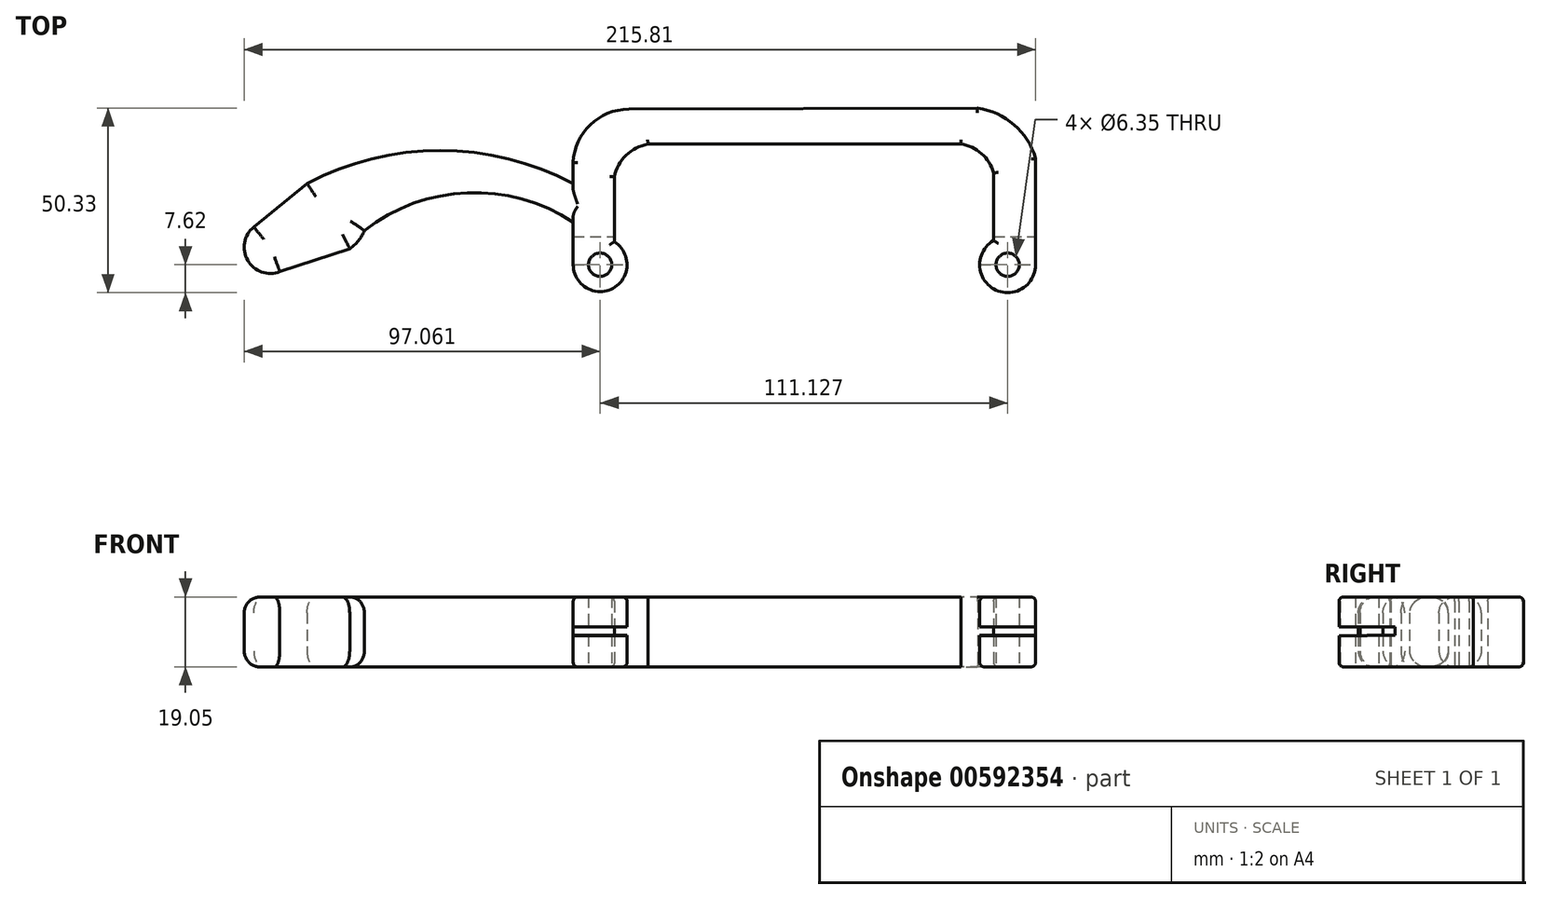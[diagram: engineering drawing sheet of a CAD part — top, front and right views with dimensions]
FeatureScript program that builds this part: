
annotation { "Feature Type Name" : "Feature", "Feature Type Description" : "" }
export const myFeature = defineFeature(function(context is Context, id is Id, definition is map)
    precondition{}
    {
        {
            var Q0;
            Q0=qCreatedBy(makeId("Top.planeOp"),FACE);
            var sketch = newSketch(context, id + "F0", { "sketchPlane" : qUnion([Q0])});
            skArc(sketch, "E0", {"start": v(-64.35, 0) * mm, "mid": v(-53.45, -6.42) * mm, "end": v(-53.12, 6.22) * mm});
            skArc(sketch, "E1", {"start": v(50.28, 6.58) * mm, "mid": v(50.32, -6.6) * mm, "end": v(61.74, 0) * mm});
            skLineSegment(sketch, "E2", {"start": v(-49.2, 42.4) * mm, "end": v(45.92, 42.71) * mm});
            skLineSegment(sketch, "E3", {"start": v(-64.35, 0) * mm, "end": v(-64.36, 11.6) * mm});
            skLineSegment(sketch, "E4", {"start": v(61.74, 0) * mm, "end": v(61.74, 29) * mm});
            skLineSegment(sketch, "E5", {"start": v(-53.12, 6.22) * mm, "end": v(-53.12, 23.94) * mm});
            skLineSegment(sketch, "E6", {"start": v(50.28, 6.58) * mm, "end": v(50.28, 25.02) * mm});
            skLineSegment(sketch, "E7", {"start": v(-43.96, 32.9) * mm, "end": v(41.35, 32.9) * mm});
            skArc(sketch, "E8", {"start": v(-43.96, 32.9) * mm, "mid": v(-49.93, 29.85) * mm, "end": v(-53.12, 23.94) * mm});
            skArc(sketch, "E9", {"start": v(50.28, 25.02) * mm, "mid": v(45.78, 31.23) * mm, "end": v(38.3, 32.9) * mm});
            skCircle(sketch, "E10", {"center": v(-57, 0) * mm, "radius": 3.18 * mm});
            skCircle(sketch, "E11", {"center": v(54.12, 0) * mm, "radius": 3.18 * mm});
            skArc(sketch, "E12", {"start": v(-49.2, 42.4) * mm, "mid": v(-59.68, 38.2) * mm, "end": v(-64.37, 27.92) * mm});
            skPoint(sketch, "E13.orphan", {"position": v(50.28, 19.35) * mm});
            skPoint(sketch, "E14.orphan", {"position": v(50.28, 4) * mm});
            skPoint(sketch, "E15.orphan", {"position": v(-53.12, 32.9) * mm});
            skPoint(sketch, "E16.orphan", {"position": v(-53.12, 19.57) * mm});
            skPoint(sketch, "E17.trimOffspring.end.orphan", {"position": v(50.28, 34.71) * mm});
            skArc(sketch, "E18", {"start": v(61.74, 29) * mm, "mid": v(55.85, 38.18) * mm, "end": v(45.92, 42.71) * mm});
            skArc(sketch, "E19", {"start": v(-64.37, 22.19) * mm, "mid": v(-100.65, 31.15) * mm, "end": v(-136.94, 22.19) * mm});
            skArc(sketch, "E20", {"start": v(-125.3, 4.38) * mm, "mid": v(-122.93, 6.54) * mm, "end": v(-121.32, 9.32) * mm});
            skPoint(sketch, "E20.second.point", {"position": v(-136.94, 4.23) * mm});
            skPoint(sketch, "E20.third.point", {"position": v(-120.6, 13.98) * mm});
            skArc(sketch, "E21", {"start": v(-151.44, 10.3) * mm, "mid": v(-153.1, 1.17) * mm, "end": v(-144.36, -1.88) * mm});
            skArc(sketch, "E22", {"start": v(-64.36, 11.6) * mm, "mid": v(-93.2, 19.62) * mm, "end": v(-121.32, 9.32) * mm});
            skLineSegment(sketch, "E23", {"start": v(-151.44, 10.3) * mm, "end": v(-136.94, 22.19) * mm});
            skLineSegment(sketch, "E24", {"start": v(-145.09, -2.12) * mm, "end": v(-125.3, 4.38) * mm});
            skLineSegment(sketch, "E25.trimOffspring", {"start": v(-64.37, 22.19) * mm, "end": v(-64.37, 27.92) * mm});
            skSolve(sketch);
        }
        {
            var Q0;
            Q0 = qSketchRegion(id + "F0", true);
            extrude(context, id + "F1", {"entities" : qUnion([Q0]), "depth" : 19.05 * mm, "offsetDistance" : 25.4 * mm});
        }
        {
            var Q0;
            Q0=makeQuery(id+"F1.opExtrude","CAP_EDGE",EDGE,{"disambiguationData":[OSD([sQuery(id+"F0.wireOp",EDGE,"E22")])],"isStart":false});
            var Q1;
            Q1=makeQuery(id+"F1.opExtrude","CAP_EDGE",EDGE,{"disambiguationData":[OSD([sQuery(id+"F0.wireOp",EDGE,"E20")])],"isStart":false});
            var Q2;
            Q2=makeQuery(id+"F1.opExtrude","CAP_EDGE",EDGE,{"disambiguationData":[OSD([sQuery(id+"F0.wireOp",EDGE,"E23")])],"isStart":false});
            var Q3;
            Q3=makeQuery(id+"F1.opExtrude","CAP_EDGE",EDGE,{"disambiguationData":[OSD([sQuery(id+"F0.wireOp",EDGE,"E21")])],"isStart":false});
            var Q4;
            Q4=makeQuery(id+"F1.opExtrude","CAP_EDGE",EDGE,{"disambiguationData":[OSD([sQuery(id+"F0.wireOp",EDGE,"E19")])],"isStart":false});
            fillet(context, id + "F2", {"entities" : qUnion([Q0, Q1, Q2, Q3, Q4]), "radius" : 4.32 * mm, "tangentPropagation" : true, "allowEdgeOverflow" : false});
        }
        {
            var Q0;
            Q0=makeQuery(id+"F1.opExtrude","CAP_EDGE",EDGE,{"disambiguationData":[OSD([sQuery(id+"F0.wireOp",EDGE,"E24")])],"isStart":true});
            var Q1;
            Q1=makeQuery(id+"F1.opExtrude","CAP_EDGE",EDGE,{"disambiguationData":[OSD([sQuery(id+"F0.wireOp",EDGE,"E20")])],"isStart":true});
            var Q2;
            Q2=makeQuery(id+"F1.opExtrude","CAP_EDGE",EDGE,{"disambiguationData":[OSD([sQuery(id+"F0.wireOp",EDGE,"E22")])],"isStart":true});
            var Q3;
            Q3=makeQuery(id+"F1.opExtrude","CAP_EDGE",EDGE,{"disambiguationData":[OSD([sQuery(id+"F0.wireOp",EDGE,"E21")])],"isStart":true});
            var Q4;
            Q4=makeQuery(id+"F1.opExtrude","CAP_EDGE",EDGE,{"disambiguationData":[OSD([sQuery(id+"F0.wireOp",EDGE,"E19")])],"isStart":true});
            var Q5;
            Q5=makeQuery(id+"F1.opExtrude","CAP_EDGE",EDGE,{"disambiguationData":[OSD([sQuery(id+"F0.wireOp",EDGE,"E23")])],"isStart":true});
            fillet(context, id + "F3", {"entities" : qUnion([Q0, Q1, Q2, Q3, Q4, Q5]), "radius" : 4.32 * mm, "tangentPropagation" : true, "allowEdgeOverflow" : false});
        }
        {
            var Q0;
            Q0=makeQuery(id+"F1.opExtrude","CAP_EDGE",EDGE,{"disambiguationData":[OSD([sQuery(id+"F0.wireOp",EDGE,"E12")])],"isStart":true});
            var Q1;
            Q1=makeQuery(id+"F1.opExtrude","CAP_EDGE",EDGE,{"disambiguationData":[OSD([sQuery(id+"F0.wireOp",EDGE,"E2")])],"isStart":true});
            var Q2;
            Q2=makeQuery(id+"F1.opExtrude","CAP_EDGE",EDGE,{"disambiguationData":[OSD([sQuery(id+"F0.wireOp",EDGE,"E6")])],"isStart":true});
            var Q3;
            Q3=makeQuery(id+"F1.opExtrude","CAP_EDGE",EDGE,{"disambiguationData":[OSD([sQuery(id+"F0.wireOp",EDGE,"E9")])],"isStart":true});
            var Q4;
            Q4=makeQuery(id+"F1.opExtrude","CAP_EDGE",EDGE,{"disambiguationData":[OSD([sQuery(id+"F0.wireOp",EDGE,"E5")])],"isStart":true});
            var Q5;
            Q5=makeQuery(id+"F1.opExtrude","CAP_EDGE",EDGE,{"disambiguationData":[OSD([sQuery(id+"F0.wireOp",EDGE,"E8")])],"isStart":true});
            var Q6;
            Q6=makeQuery(id+"F1.opExtrude","CAP_EDGE",EDGE,{"disambiguationData":[OSD([sQuery(id+"F0.wireOp",EDGE,"E7")])],"isStart":true});
            var Q7;
            Q7=makeQuery(id+"F1.opExtrude","CAP_EDGE",EDGE,{"disambiguationData":[OSD([sQuery(id+"F0.wireOp",EDGE,"E18")])],"isStart":true});
            var Q8;
            Q8=makeQuery(id+"F1.opExtrude","CAP_EDGE",EDGE,{"disambiguationData":[OSD([sQuery(id+"F0.wireOp",EDGE,"E4")])],"isStart":true});
            var Q9;
            Q9=makeQuery(id+"F1.opExtrude","CAP_EDGE",EDGE,{"disambiguationData":[OSD([sQuery(id+"F0.wireOp",EDGE,"E3")])],"isStart":true});
            var Q10;
            Q10=makeQuery(id+"F1.opExtrude","CAP_EDGE",EDGE,{"disambiguationData":[OSD([sQuery(id+"F0.wireOp",EDGE,"E0")])],"isStart":true});
            fillet(context, id + "F4", {"entities" : qUnion([Q0, Q1, Q2, Q3, Q4, Q5, Q6, Q7, Q8, Q9, Q10]), "radius" : 1.23 * mm, "tangentPropagation" : true, "allowEdgeOverflow" : false});
        }
        {
            var Q0;
            Q0=makeQuery(id+"F1.opExtrude","CAP_EDGE",EDGE,{"disambiguationData":[OSD([sQuery(id+"F0.wireOp",EDGE,"E12")])],"isStart":false});
            var Q1;
            Q1=makeQuery(id+"F1.opExtrude","CAP_EDGE",EDGE,{"disambiguationData":[OSD([sQuery(id+"F0.wireOp",EDGE,"E25.trimOffspring")])],"isStart":false});
            var Q2;
            Q2=makeQuery(id+"F1.opExtrude","CAP_EDGE",EDGE,{"disambiguationData":[OSD([sQuery(id+"F0.wireOp",EDGE,"E3")])],"isStart":false});
            var Q3;
            Q3=makeQuery(id+"F1.opExtrude","CAP_EDGE",EDGE,{"disambiguationData":[OSD([sQuery(id+"F0.wireOp",EDGE,"E0")])],"isStart":false});
            var Q4;
            Q4=makeQuery(id+"F1.opExtrude","CAP_EDGE",EDGE,{"disambiguationData":[OSD([sQuery(id+"F0.wireOp",EDGE,"E5")])],"isStart":false});
            var Q5;
            Q5=makeQuery(id+"F1.opExtrude","CAP_EDGE",EDGE,{"disambiguationData":[OSD([sQuery(id+"F0.wireOp",EDGE,"E8")])],"isStart":false});
            var Q6;
            Q6=makeQuery(id+"F1.opExtrude","CAP_EDGE",EDGE,{"disambiguationData":[OSD([sQuery(id+"F0.wireOp",EDGE,"E7")])],"isStart":false});
            var Q7;
            Q7=makeQuery(id+"F1.opExtrude","CAP_EDGE",EDGE,{"disambiguationData":[OSD([sQuery(id+"F0.wireOp",EDGE,"E2")])],"isStart":false});
            var Q8;
            Q8=makeQuery(id+"F1.opExtrude","CAP_EDGE",EDGE,{"disambiguationData":[OSD([sQuery(id+"F0.wireOp",EDGE,"E18")])],"isStart":false});
            var Q9;
            Q9=makeQuery(id+"F1.opExtrude","CAP_EDGE",EDGE,{"disambiguationData":[OSD([sQuery(id+"F0.wireOp",EDGE,"E9")])],"isStart":false});
            var Q10;
            Q10=makeQuery(id+"F1.opExtrude","CAP_EDGE",EDGE,{"disambiguationData":[OSD([sQuery(id+"F0.wireOp",EDGE,"E6")])],"isStart":false});
            var Q11;
            Q11=makeQuery(id+"F1.opExtrude","CAP_EDGE",EDGE,{"disambiguationData":[OSD([sQuery(id+"F0.wireOp",EDGE,"E1")])],"isStart":false});
            var Q12;
            Q12=makeQuery(id+"F1.opExtrude","CAP_EDGE",EDGE,{"disambiguationData":[OSD([sQuery(id+"F0.wireOp",EDGE,"E4")])],"isStart":false});
            fillet(context, id + "F5", {"entities" : qUnion([Q0, Q1, Q2, Q3, Q4, Q5, Q6, Q7, Q8, Q9, Q10, Q11, Q12]), "radius" : 1.22 * mm, "tangentPropagation" : true, "allowEdgeOverflow" : false});
        }
        {
            var Q0;
            Q0=qCreatedBy(makeId("Front.planeOp"),FACE);
            var sketch = newSketch(context, id + "F6", { "sketchPlane" : qUnion([Q0])});
            skLineSegment(sketch, "E26.bottom", {"start": v(-66.85, 10.9) * mm, "end": v(73.25, 10.9) * mm});
            skLineSegment(sketch, "E26.top", {"start": v(-66.85, 8.56) * mm, "end": v(73.25, 8.56) * mm});
            skLineSegment(sketch, "E26.left", {"start": v(-66.85, 10.9) * mm, "end": v(-66.85, 8.56) * mm});
            skLineSegment(sketch, "E26.right", {"start": v(73.25, 10.9) * mm, "end": v(73.25, 8.56) * mm});
            skSolve(sketch);
        }
        {
            var Q0;
            Q0 = qSketchRegion(id + "F6", true);
            extrude(context, id + "F7", {"entities" : qUnion([Q0]), "operationType" : NewBodyOperationType.REMOVE, "oppositeDirection" : true, "depth" : 7.62 * mm, "offsetDistance" : 25.4 * mm});
        }
        {
            var Q0;
            Q0=qCreatedBy(makeId("Front.planeOp"),FACE);
            var sketch = newSketch(context, id + "F8", { "sketchPlane" : qUnion([Q0])});
            skLineSegment(sketch, "E27.bottom", {"start": v(-69.68, 10.93) * mm, "end": v(76.08, 10.93) * mm});
            skLineSegment(sketch, "E27.top", {"start": v(-69.68, 8.54) * mm, "end": v(76.08, 8.54) * mm});
            skLineSegment(sketch, "E27.left", {"start": v(-69.68, 10.93) * mm, "end": v(-69.68, 8.54) * mm});
            skLineSegment(sketch, "E27.right", {"start": v(76.08, 10.93) * mm, "end": v(76.08, 8.54) * mm});
            skSolve(sketch);
        }
        {
            var Q0;
            Q0 = qSketchRegion(id + "F8", true);
            extrude(context, id + "F9", {"entities" : qUnion([Q0]), "operationType" : NewBodyOperationType.REMOVE, "depth" : 25.4 * mm, "offsetDistance" : 25.4 * mm});
        }
    });
